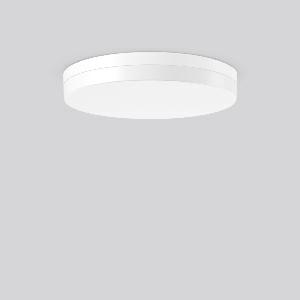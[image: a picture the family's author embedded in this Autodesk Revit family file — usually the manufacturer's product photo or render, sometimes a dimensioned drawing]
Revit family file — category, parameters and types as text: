
# Revit family: flat_slim_round_312634_002_76_748a
name_source: partatom
category: Lighting Fixtures
units: mm (PartAtom-declared; Revit-internal decimal feet)

## family parameters
Cut with Voids When Loaded = No
Host = Face
Light Source = No
Part Type = Normal
Room Calculation Point = No
Round Connector Dimension = Use Diameter
Shared = No

## types (1)
- MultiLumen 1 830 (1 x LED Modul 830, 3450 lm, 3000)
    Apparent Load = 26 VA
    CIE Flux Codes = 40 71 90 84 100
    Color Rendering = 80
    Color Temperature = 3000
    Default Elevation = 1800 mm
    Height = 70 mm
    Lamp = 1 x LED Modul 830
    Lamp Light Flux = 3450 lm
    Lamp count = 1
    Length = 480 mm
    Lifetime = 50000 h
    Luminous efficacy = 133 lm/W
    Manufacturer = RZB
    ModVariant = No
    Model = 312634.002.76
    Mounting Place = Ceiling
    Mounting Type = Surface mounted
    Number of Poles = 1
    OnlyDefault = Yes
    Power Factor = 1
    Product Name = FLAT SLIM round
    Product group = Surface mounted ceiling and wall luminaires
    ProductGroupID = 305
    Protection Class = Protection class I
    Protection Degree = Degree of protection
    RLX_Detail_Level = 1
    RLX_Emergency_Light_Flux = 0 lm
    RLX_Emergency_Type = 0
    RLX_Emergency_Type_DB = No
    RlxData = <blob elided: 20981 chars, md5=310ae297>
    Socket = socket
    Standby Power = 0 W
    System Light Flux = 3450 lm
    System Power = 26 W
    Type Comments = MultiLumen 1 830
    Type Image = 312633.002.jpg
    URL = http://relux.com
    VarID = multilumen_1_830
    Voltage = 0 V
    Weight = 0.00 kg
    Width = 0 mm  [stored 0 ft]

note: [stored X ft] marks values corroborated as IEEE doubles in the binary element streams (Revit-internal decimal feet)

## geometry (parser evidence)
native form markers: Blend x4, Sweep x14
no freeform markers — native parametric forms only
